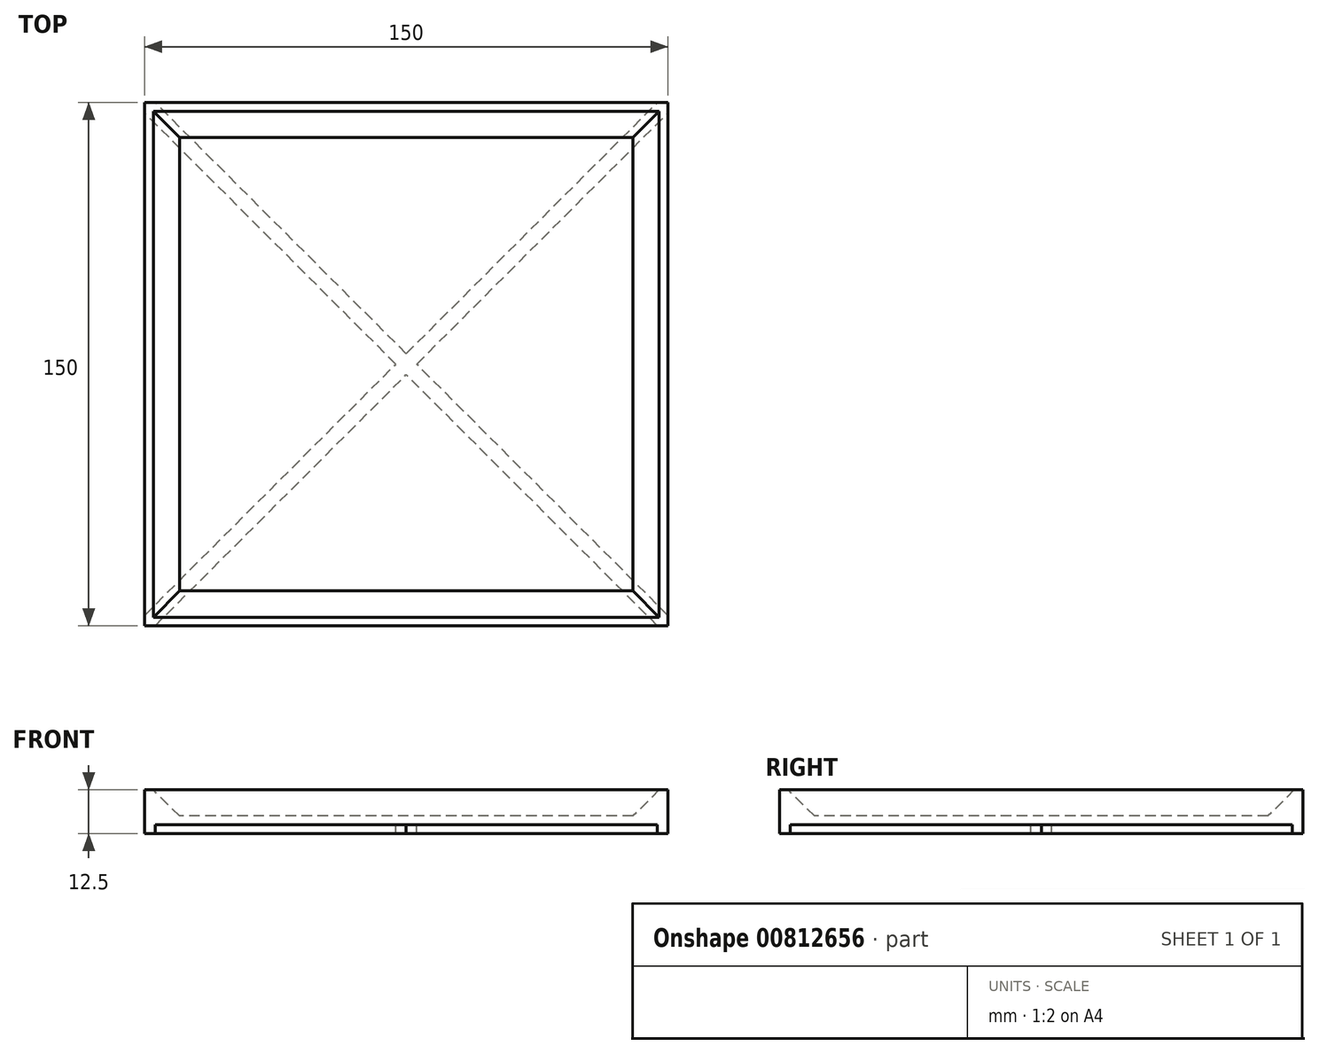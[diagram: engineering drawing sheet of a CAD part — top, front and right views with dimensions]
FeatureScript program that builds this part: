
annotation { "Feature Type Name" : "Feature", "Feature Type Description" : "" }
export const myFeature = defineFeature(function(context is Context, id is Id, definition is map)
    precondition{}
    {
        {
            var Q0;
            Q0=qCreatedBy(makeId("Top.planeOp"),FACE);
            var sketch = newSketch(context, id + "F0", { "sketchPlane" : qUnion([Q0])});
            skLineSegment(sketch, "E0.bottom", {"start": v(75, -75) * mm, "end": v(-75, -75) * mm});
            skLineSegment(sketch, "E0.top", {"start": v(75, 75) * mm, "end": v(-75, 75) * mm});
            skLineSegment(sketch, "E0.left", {"start": v(75, -75) * mm, "end": v(75, 75) * mm});
            skLineSegment(sketch, "E0.right", {"start": v(-75, -75) * mm, "end": v(-75, 75) * mm});
            skPoint(sketch, "E0.middle", {"position": v(0, 0) * mm});
            skSolve(sketch);
        }
        {
            var Q0;
            Q0 = qSketchRegion(id + "F0", true);
            extrude(context, id + "F1", {"entities" : qUnion([Q0]), "depth" : 10 * mm, "offsetDistance" : 25 * mm});
        }
        {
            var Q0;
            Q0=makeQuery(id+"F1.opExtrude","CAP_FACE",FACE,{"disambiguationData":[OSD([sQuery(id+"F0.wireOp",EDGE,"E0.bottom"),sQuery(id+"F0.wireOp",EDGE,"E0.top"),sQuery(id+"F0.wireOp",EDGE,"E0.left"),sQuery(id+"F0.wireOp",EDGE,"E0.right")])],"isStart":false});
            shell(context, id + "F2", {"entities" : qUnion([Q0]), "thickness" : 2.5 * mm});
        }
        {
            var Q0;
            {var subQ0=sQuery(id+"F0.wireOp",EDGE,"E0.right");Q0=makeQuery(id+"F2.opShell","OFFSET_EDGE",EDGE,{"disambiguationData":[OSD([subQ0]),TDD([makeQuery(id+"F1.opExtrude","CAP_EDGE",EDGE,{"disambiguationData":[OSD([subQ0])],"isStart":true})])]});}
            var Q1;
            {var subQ0=sQuery(id+"F0.wireOp",EDGE,"E0.top");Q1=makeQuery(id+"F2.opShell","OFFSET_EDGE",EDGE,{"disambiguationData":[OSD([subQ0]),TDD([makeQuery(id+"F1.opExtrude","CAP_EDGE",EDGE,{"disambiguationData":[OSD([subQ0])],"isStart":true})])]});}
            var Q2;
            {var subQ0=sQuery(id+"F0.wireOp",EDGE,"E0.left");Q2=makeQuery(id+"F2.opShell","OFFSET_EDGE",EDGE,{"disambiguationData":[OSD([subQ0]),TDD([makeQuery(id+"F1.opExtrude","CAP_EDGE",EDGE,{"disambiguationData":[OSD([subQ0])],"isStart":true})])]});}
            var Q3;
            {var subQ0=sQuery(id+"F0.wireOp",EDGE,"E0.bottom");Q3=makeQuery(id+"F2.opShell","OFFSET_EDGE",EDGE,{"disambiguationData":[OSD([subQ0]),TDD([makeQuery(id+"F1.opExtrude","CAP_EDGE",EDGE,{"disambiguationData":[OSD([subQ0])],"isStart":true})])]});}
            chamfer(context, id + "F3", {"entities" : qUnion([Q0, Q1, Q2, Q3]), "width" : 7.5 * mm, "tangentPropagation" : true});
        }
        {
            var Q0;
            Q0=makeQuery(id+"F1.opExtrude","CAP_FACE",FACE,{"disambiguationData":[OSD([sQuery(id+"F0.wireOp",EDGE,"E0.bottom"),sQuery(id+"F0.wireOp",EDGE,"E0.top"),sQuery(id+"F0.wireOp",EDGE,"E0.left"),sQuery(id+"F0.wireOp",EDGE,"E0.right")])],"isStart":true});
            var sketch = newSketch(context, id + "F4", { "sketchPlane" : qUnion([Q0])});
            skLineSegment(sketch, "E1", {"start": v(-72, 75) * mm, "end": v(0, 3) * mm});
            skLineSegment(sketch, "E2", {"start": v(-75, 72) * mm, "end": v(-3, 0) * mm});
            skLineSegment(sketch, "E3", {"start": v(72, 75) * mm, "end": v(0, 3) * mm});
            skLineSegment(sketch, "E4", {"start": v(75, 72) * mm, "end": v(3, 0) * mm});
            skLineSegment(sketch, "E5.trimOffspring", {"start": v(-3, 0) * mm, "end": v(-75, -72) * mm});
            skLineSegment(sketch, "E6.trimOffspring", {"start": v(3, 0) * mm, "end": v(75, -72) * mm});
            skLineSegment(sketch, "E7.trimOffspring", {"start": v(0, -3) * mm, "end": v(-72, -75) * mm});
            skLineSegment(sketch, "E8.trimOffspring", {"start": v(0, -3) * mm, "end": v(72, -75) * mm});
            skSolve(sketch);
        }
        {
            var Q0;
            {var subQ3=sQuery(id+"F4.wireOp",EDGE,"E1");Q0=makeQuery(id+"F4.imprint","IMPRINT",FACE,{"disambiguationData":[TD([[makeQuery(id+"F4.imprint","IMPRINT",EDGE,{"derivedFrom":subQ3}),-1.0]])]});}
            extrude(context, id + "F5", {"entities" : qUnion([Q0]), "operationType" : NewBodyOperationType.ADD, "depth" : 2.5 * mm, "offsetDistance" : 25 * mm});
        }
    });
